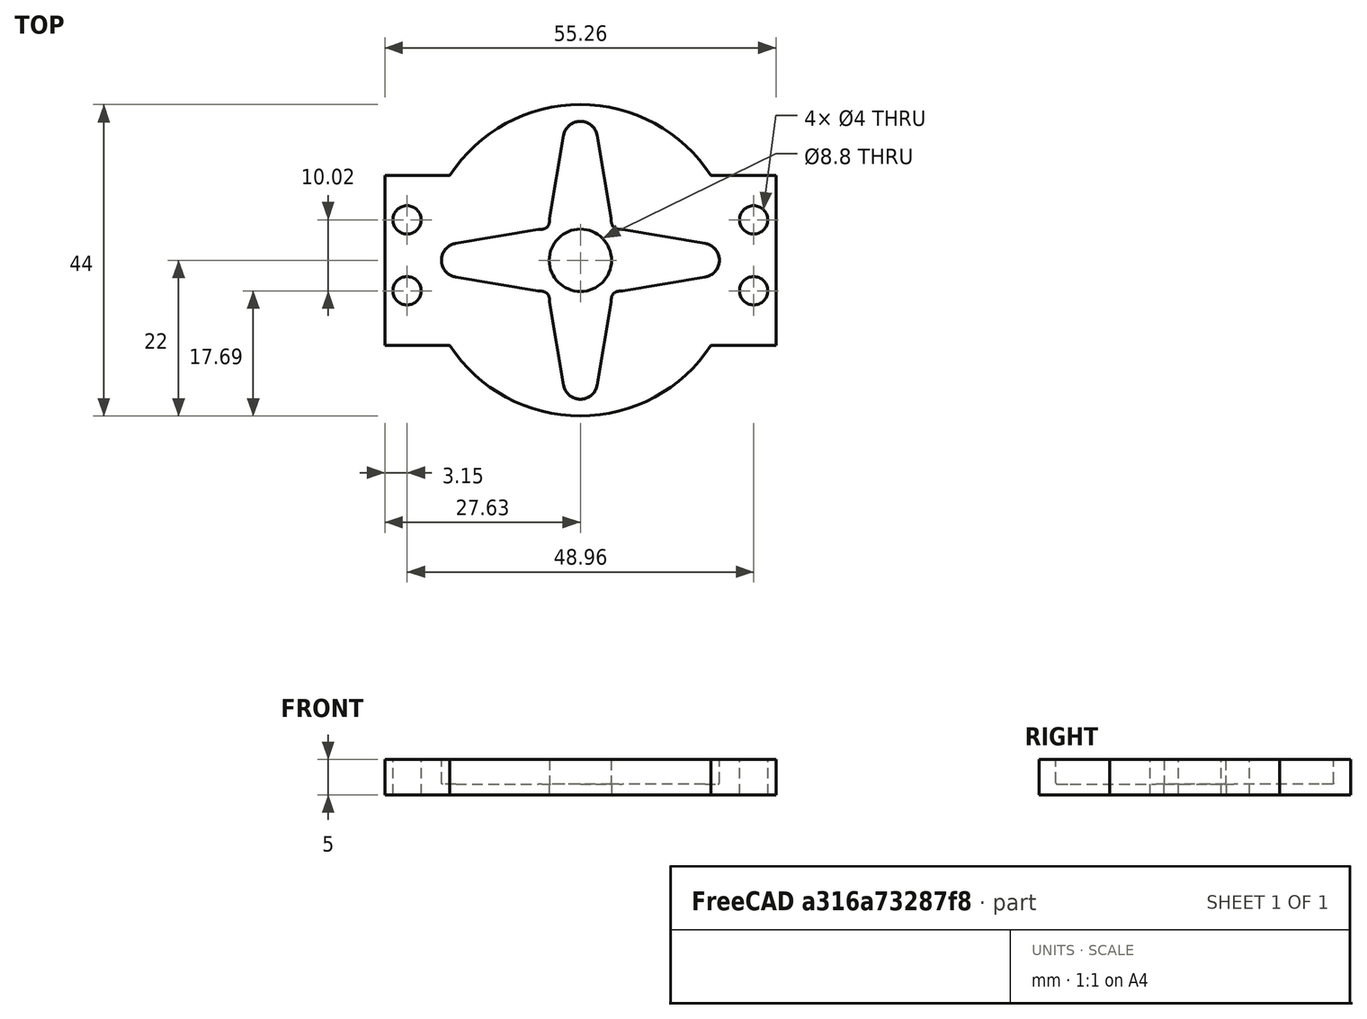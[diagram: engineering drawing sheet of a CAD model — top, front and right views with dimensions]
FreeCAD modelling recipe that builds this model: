
FCSTD DOCUMENT  (FreeCAD 0.16R6700 (Git))
Label: pieza4V1
License: CreativeCommons Attribution-ShareAlike
LicenseURL: http://creativecommons.org/licenses/by-sa/4.0/
objects: Part::Cylinder×5, Part::Cut×5, Part::Feature×2, Part::Box×1, Part::MultiFuse×1
note: 14 computed .brp shape members not serialized (recipe doc carries the construction recipe); baked Part::Feature solids carry a one-line shape summary decoded from their .brp

FEATURE [Part::Box] Box  label="Cubo"
  Height = 5
  Length = 55.26
  Width = 24
FEATURE [Part::Feature] Fusion001  label="csForHuecoHorm"
  Placement = pos=(27.63,12,6.5) rot=(1,0,0;3.14159rad)
  shape: bbox 39.25 x 39.25 x 14.4 mm, 108 faces (baked)
FEATURE [Part::Cylinder] Cylinder  label="Cilindro"
  Angle = 360
  Height = 5
  Placement = pos=(27.63,12,0) rot=(0,0,1;0rad)
  Radius = 22
FEATURE [Part::MultiFuse] Fusion
  Shapes = -> [Cylinder,Box]
FEATURE [Part::Cut] Cut
  Base = -> Fusion
  Tool = -> Fusion001
FEATURE [Part::Cylinder] Cylinder004  label="Cilindro004"
  Angle = 360
  Height = 15
  Placement = pos=(3.15,17.71,-6) rot=(0,0,1;0rad)
  Radius = 2
FEATURE [Part::Cylinder] Cylinder005  label="Cilindro005"
  Angle = 360
  Height = 15
  Placement = pos=(52.11,7.69,-6) rot=(0,0,1;0rad)
  Radius = 2
FEATURE [Part::Cylinder] Cylinder006  label="Cilindro006"
  Angle = 360
  Height = 15
  Placement = pos=(3.15,7.69,-6) rot=(0,0,1;0rad)
  Radius = 2
FEATURE [Part::Cylinder] Cylinder007  label="Cilindro007"
  Angle = 360
  Height = 15
  Placement = pos=(52.11,17.71,-6) rot=(0,0,1;0rad)
  Radius = 2
FEATURE [Part::Cut] Cut001
  Base = -> Cut
  Tool = -> Cylinder004
FEATURE [Part::Cut] Cut002
  Base = -> Cut001
  Tool = -> Cylinder005
FEATURE [Part::Cut] Cut003
  Base = -> Cut002
  Tool = -> Cylinder006
FEATURE [Part::Cut] Cut004  label="Pieza4v1"
  Base = -> Cut003
  Tool = -> Cylinder007
FEATURE [Part::Feature] Cut004001  label="csPieza4v1"
  shape: bbox 55.26 x 44 x 5 mm, 84 faces (baked)
